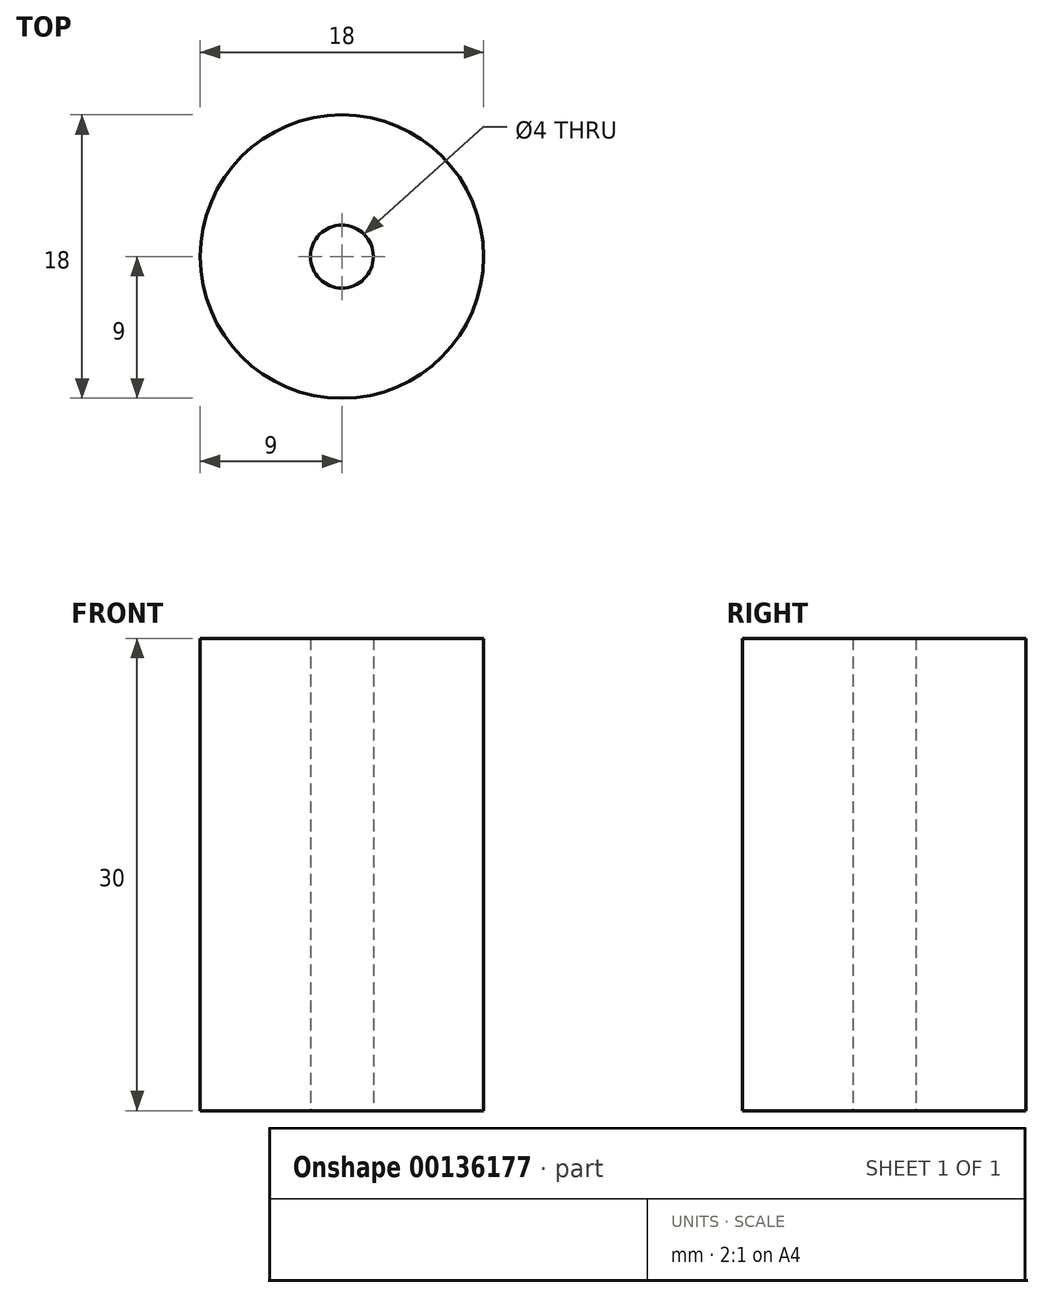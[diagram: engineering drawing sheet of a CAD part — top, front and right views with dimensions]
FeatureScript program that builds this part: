
annotation { "Feature Type Name" : "Feature", "Feature Type Description" : "" }
export const myFeature = defineFeature(function(context is Context, id is Id, definition is map)
    precondition{}
    {
        {
            var Q0;
            Q0=qCreatedBy(makeId("Top.planeOp"),FACE);
            var sketch = newSketch(context, id + "F0", { "sketchPlane" : qUnion([Q0])});
            skCircle(sketch, "E0", {"center": v(0, 0) * mm, "radius": 9 * mm});
            skCircle(sketch, "E1", {"center": v(0, 0) * mm, "radius": 2 * mm});
            skSolve(sketch);
        }
        {
            var Q0;
            Q0=makeQuery(id+"F0.imprint","IMPRINT",FACE,{"disambiguationData":[TD([[makeQuery(id+"F0.imprint","IMPRINT",EDGE,{"derivedFrom":sQuery(id+"F0.wireOp",EDGE,"E0")}),1.0]])]});
            extrude(context, id + "F1", {"entities" : qUnion([Q0]), "depth" : 30 * mm});
        }
    });
